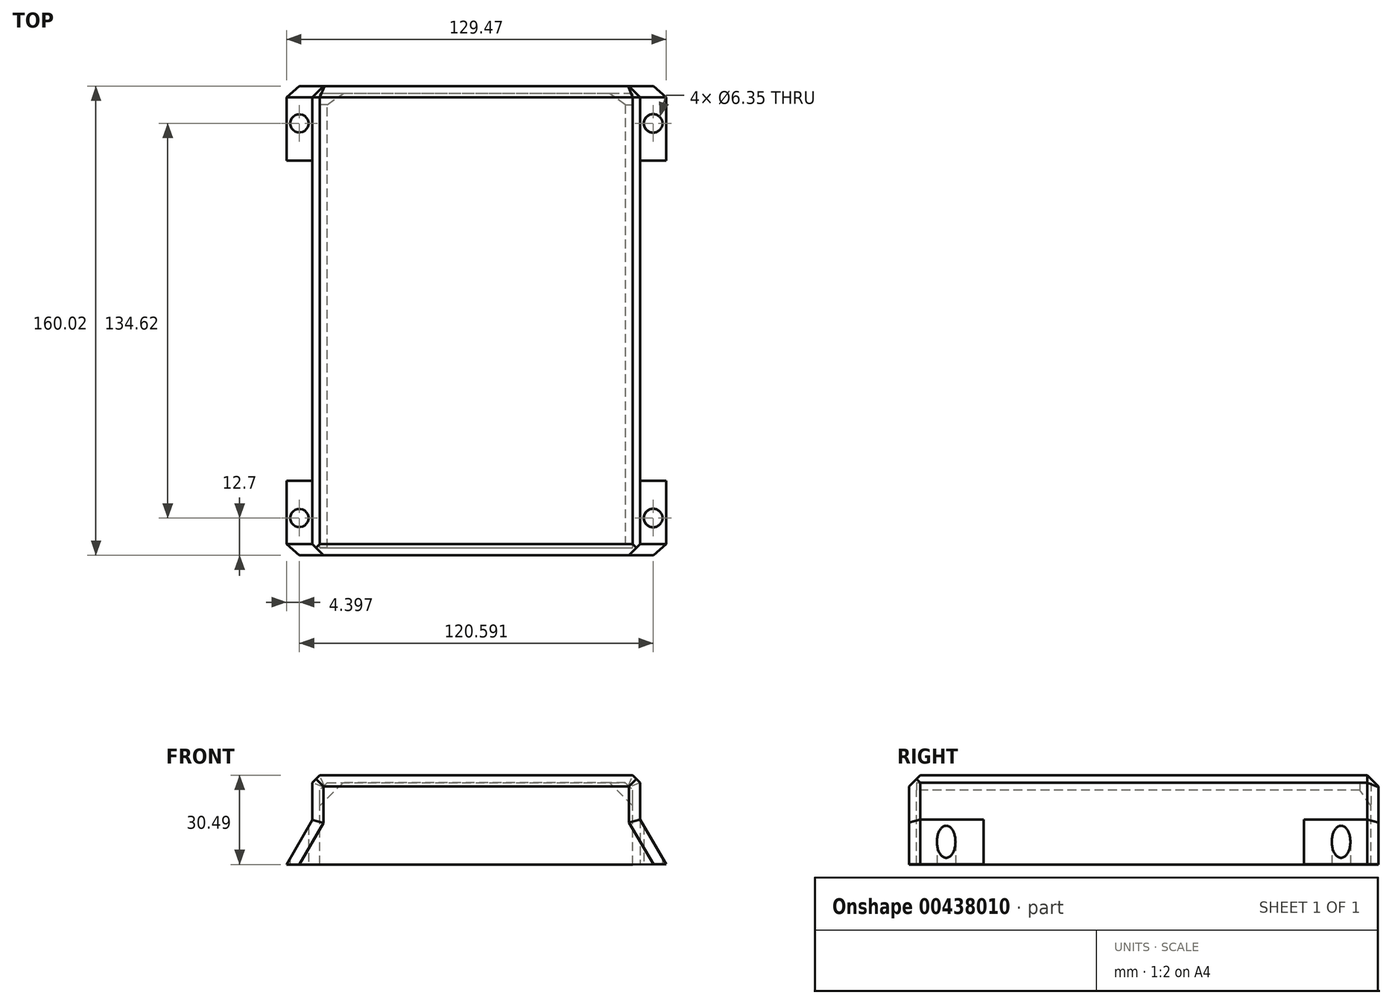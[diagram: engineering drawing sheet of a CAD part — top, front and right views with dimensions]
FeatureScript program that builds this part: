
annotation { "Feature Type Name" : "Feature", "Feature Type Description" : "" }
export const myFeature = defineFeature(function(context is Context, id is Id, definition is map)
    precondition{}
    {
        {
            var Q0;
            Q0=qCreatedBy(makeId("Front.planeOp"),FACE);
            var sketch = newSketch(context, id + "F0", { "sketchPlane" : qUnion([Q0])});
            skLineSegment(sketch, "E0.bottom", {"start": v(-84.5, 54.95) * mm, "end": v(27.26, 54.95) * mm});
            skLineSegment(sketch, "E0.top", {"start": v(-84.5, 24.47) * mm, "end": v(-81.96, 24.47) * mm});
            skLineSegment(sketch, "E0.left", {"start": v(-84.5, 54.95) * mm, "end": v(-84.5, 39.7) * mm});
            skLineSegment(sketch, "E0.right", {"start": v(27.26, 54.95) * mm, "end": v(27.26, 39.8) * mm});
            skLineSegment(sketch, "E1", {"start": v(-84.5, 39.7) * mm, "end": v(-93.3, 24.47) * mm});
            skLineSegment(sketch, "E2", {"start": v(-93.3, 24.47) * mm, "end": v(-84.5, 24.47) * mm});
            skLineSegment(sketch, "E3.MirrorCS", {"start": v(27.26, 39.8) * mm, "end": v(36.17, 24.5) * mm});
            skPoint(sketch, "E4.start.orphan", {"position": v(-28.62, 24.47) * mm});
            skLineSegment(sketch, "E5", {"start": v(-81.96, 24.47) * mm, "end": v(-81.96, 52.4) * mm});
            skLineSegment(sketch, "E6", {"start": v(-81.96, 52.4) * mm, "end": v(24.72, 52.4) * mm});
            skLineSegment(sketch, "E7.MirrorCS", {"start": v(24.72, 24.46) * mm, "end": v(24.72, 52.4) * mm});
            skLineSegment(sketch, "E8", {"start": v(24.72, 24.46) * mm, "end": v(36.17, 24.5) * mm});
            skSolve(sketch);
        }
        {
            var Q0;
            Q0=makeQuery(id+"F0.imprint","IMPRINT",FACE,{"disambiguationData":[TD([[makeQuery(id+"F0.imprint","IMPRINT",EDGE,{"derivedFrom":sQuery(id+"F0.wireOp",EDGE,"E0.bottom")}),-1.0]])]});
            extrude(context, id + "F1", {"entities" : qUnion([Q0]), "depth" : 160.02 * mm});
        }
        {
            var Q0;
            Q0=makeQuery(id+"F1.opExtrude","SWEPT_EDGE",EDGE,{"disambiguationData":[OSD([sQuery(id+"F0.wireOp",EDGE,"E0.bottom"),sQuery(id+"F0.wireOp",EDGE,"E0.left")])]});
            var Q1;
            Q1=makeQuery(id+"F1.opExtrude","SWEPT_EDGE",EDGE,{"disambiguationData":[OSD([sQuery(id+"F0.wireOp",EDGE,"E6"),sQuery(id+"F0.wireOp",EDGE,"E7.MirrorCS")])]});
            var Q2;
            Q2=makeQuery(id+"F1.opExtrude","SWEPT_EDGE",EDGE,{"disambiguationData":[OSD([sQuery(id+"F0.wireOp",EDGE,"E5"),sQuery(id+"F0.wireOp",EDGE,"E6")])]});
            var Q3;
            Q3=makeQuery(id+"F1.opExtrude","SWEPT_EDGE",EDGE,{"disambiguationData":[OSD([sQuery(id+"F0.wireOp",EDGE,"E0.bottom"),sQuery(id+"F0.wireOp",EDGE,"E0.right")])]});
            chamfer(context, id + "F2", {"entities" : qUnion([Q0, Q1, Q2, Q3]), "width" : 2.54 * mm, "tangentPropagation" : true});
        }
        {
            var Q0;
            Q0=makeQuery(id+"F2DOVUVanhk7CML_1.boolean.opBoolean","MERGE",FACE,{"derivedFrom":[makeQuery(id+"F1.opExtrude","SWEPT_FACE",FACE,{"disambiguationData":[OSD([sQuery(id+"F0.wireOp",EDGE,"E0.top"),sQuery(id+"F0.wireOp",EDGE,"E2")])]}),makeQuery(id+"F1.opExtrude","SWEPT_FACE",FACE,{"disambiguationData":[OSD([sQuery(id+"F0.wireOp",EDGE,"2e7b0b60-ae61-4e8e-ab8d-efaa882fdc4c.trimOffspring")])]}),makeQuery(id+"F2DOVUVanhk7CML_1.opExtrude","SWEPT_FACE",FACE,{"disambiguationData":[OSD([sQuery(id+"F7f3OZNVjXZdd6c_1.wireOp",EDGE,"704NCxIe-Shb7-Pqu0-nzQe-OlCcpkSPJt9R.bottom")])]})]});
            var sketch = newSketch(context, id + "F3", { "sketchPlane" : qUnion([Q0])});
            skLineSegment(sketch, "E9.left", {"start": v(-99.5, 134.62) * mm, "end": v(-99.5, 33.02) * mm});
            skLineSegment(sketch, "E10.MirrorCS", {"start": v(42.26, 134.62) * mm, "end": v(42.26, 33.02) * mm});
            skLineSegment(sketch, "E11.bottom", {"start": v(-99.5, 134.62) * mm, "end": v(-84.5, 134.62) * mm});
            skLineSegment(sketch, "E11.top", {"start": v(-99.5, 25.4) * mm, "end": v(-84.5, 25.4) * mm});
            skLineSegment(sketch, "E11.left", {"start": v(-99.5, 134.62) * mm, "end": v(-99.5, 25.4) * mm});
            skLineSegment(sketch, "E11.right", {"start": v(-84.5, 134.62) * mm, "end": v(-84.5, 25.4) * mm});
            skLineSegment(sketch, "E12.bottom", {"start": v(42.26, 134.62) * mm, "end": v(27.26, 134.62) * mm});
            skLineSegment(sketch, "E12.top", {"start": v(42.26, 25.4) * mm, "end": v(27.26, 25.4) * mm});
            skLineSegment(sketch, "E12.left", {"start": v(42.26, 134.62) * mm, "end": v(42.26, 25.4) * mm});
            skLineSegment(sketch, "E12.right", {"start": v(27.26, 134.62) * mm, "end": v(27.26, 25.4) * mm});
            skSolve(sketch);
        }
        {
            var Q0;
            Q0=makeQuery(id+"F3.imprint","IMPRINT",FACE,{"disambiguationData":[TD([[makeQuery(id+"F3.imprint","IMPRINT",EDGE,{"derivedFrom":sQuery(id+"F3.wireOp",EDGE,"E9.bottom")}),-1.0]])]});
            var Q1;
            {var subQ0=sQuery(id+"F3.wireOp",EDGE,"E10.MirrorCS");Q1=makeQuery(id+"F3.imprint","IMPRINT",FACE,{"disambiguationData":[TD([[makeQuery(id+"F3.imprint","IMPRINT",EDGE,{"derivedFrom":subQ0}),-1.0]])]});}
            extrude(context, id + "F4", {"entities" : qUnion([Q0, Q1]), "operationType" : NewBodyOperationType.REMOVE, "oppositeDirection" : true, "depth" : 25.4 * mm});
        }
        {
            var Q0;
            Q0=makeQuery(id+"F3.imprint","IMPRINT",FACE,{"disambiguationData":[TD([[makeQuery(id+"F3.imprint","IMPRINT",EDGE,{"derivedFrom":sQuery(id+"F3.wireOp",EDGE,"E11.bottom")}),-1.0]])]});
            var Q1;
            Q1=makeQuery(id+"F3.imprint","IMPRINT",FACE,{"disambiguationData":[TD([[makeQuery(id+"F3.imprint","IMPRINT",EDGE,{"derivedFrom":sQuery(id+"F3.wireOp",EDGE,"E12.bottom")}),1.0]])]});
            extrude(context, id + "F5", {"entities" : qUnion([Q0, Q1]), "operationType" : NewBodyOperationType.REMOVE, "oppositeDirection" : true, "depth" : 25.4 * mm});
        }
        {
            var Q0;
            Q0=makeQuery(id+"F2DOVUVanhk7CML_1.boolean.opBoolean","MERGE",FACE,{"derivedFrom":[makeQuery(id+"F1.opExtrude","SWEPT_FACE",FACE,{"disambiguationData":[OSD([sQuery(id+"F0.wireOp",EDGE,"E0.top"),sQuery(id+"F0.wireOp",EDGE,"E2")])]}),makeQuery(id+"F1.opExtrude","SWEPT_FACE",FACE,{"disambiguationData":[OSD([sQuery(id+"F0.wireOp",EDGE,"2e7b0b60-ae61-4e8e-ab8d-efaa882fdc4c.trimOffspring")])]}),makeQuery(id+"F2DOVUVanhk7CML_1.opExtrude","SWEPT_FACE",FACE,{"disambiguationData":[OSD([sQuery(id+"F7f3OZNVjXZdd6c_1.wireOp",EDGE,"704NCxIe-Shb7-Pqu0-nzQe-OlCcpkSPJt9R.bottom")])]})]});
            var sketch = newSketch(context, id + "F6", { "sketchPlane" : qUnion([Q0])});
            skCircle(sketch, "E13", {"center": v(-88.9, 147.32) * mm, "radius": 3.18 * mm});
            skPoint(sketch, "E13.centerSnap0", {"position": v(-93.3, 147.32) * mm});
            skPoint(sketch, "E13.centerSnap1", {"position": v(-88.9, 134.62) * mm});
            skCircle(sketch, "E14", {"center": v(-88.9, 12.7) * mm, "radius": 3.18 * mm});
            skPoint(sketch, "E14.centerSnap0", {"position": v(-88.9, 25.4) * mm});
            skPoint(sketch, "E14.centerSnap1", {"position": v(-93.3, 12.7) * mm});
            skSolve(sketch);
        }
        {
            var Q0;
            Q0=makeQuery(id+"F6.imprint","IMPRINT",FACE,{"disambiguationData":[TD([[makeQuery(id+"F6.imprint","IMPRINT",EDGE,{"derivedFrom":sQuery(id+"F6.wireOp",EDGE,"E14")}),1.0]])]});
            var Q1;
            Q1=makeQuery(id+"F6.imprint","IMPRINT",FACE,{"disambiguationData":[TD([[makeQuery(id+"F6.imprint","IMPRINT",EDGE,{"derivedFrom":sQuery(id+"F6.wireOp",EDGE,"E13")}),1.0]])]});
            var Q2;
            Q2=makeQuery(id+"FXtNLgF4TMoL3fm_1.imprint","IMPRINT",FACE,{"disambiguationData":[TD([[makeQuery(id+"FXtNLgF4TMoL3fm_1.imprint","IMPRINT",EDGE,{"derivedFrom":sQuery(id+"FXtNLgF4TMoL3fm_1.wireOp",EDGE,"AvXykiR3-Juc4-Uzjr-7NnA-D4NbyHo4XRPa")}),1.0]])]});
            var Q3;
            Q3=makeQuery(id+"FY5yyZJvRh9AwFM_1.imprint","IMPRINT",FACE,{"disambiguationData":[TD([[makeQuery(id+"FY5yyZJvRh9AwFM_1.imprint","IMPRINT",EDGE,{"derivedFrom":sQuery(id+"FY5yyZJvRh9AwFM_1.wireOp",EDGE,"1o40Q4Pv-ev4r-qfsh-RZnV-3lQHRS0gfTlM")}),1.0]])]});
            extrude(context, id + "F7", {"entities" : qUnion([Q0, Q1, Q2, Q3]), "operationType" : NewBodyOperationType.REMOVE, "oppositeDirection" : true, "depth" : 25.4 * mm});
        }
        {
            var Q0;
            Q0=makeQuery(id+"F1.opExtrude","CAP_FACE",FACE,{"disambiguationData":[OSD([sQuery(id+"F0.wireOp",EDGE,"E0.bottom"),sQuery(id+"F0.wireOp",EDGE,"E0.top"),sQuery(id+"F0.wireOp",EDGE,"E0.left"),sQuery(id+"F0.wireOp",EDGE,"E0.right"),sQuery(id+"F0.wireOp",EDGE,"E1"),sQuery(id+"F0.wireOp",EDGE,"E2"),sQuery(id+"F0.wireOp",EDGE,"E3.MirrorCS"),sQuery(id+"F0.wireOp",EDGE,"E5"),sQuery(id+"F0.wireOp",EDGE,"E6"),sQuery(id+"F0.wireOp",EDGE,"E7.MirrorCS"),sQuery(id+"F0.wireOp",EDGE,"E8")])],"isStart":false});
            var sketch = newSketch(context, id + "F8", { "sketchPlane" : qUnion([Q0])});
            skLineSegment(sketch, "E15.bottom", {"start": v(-81.96, 24.47) * mm, "end": v(24.72, 24.47) * mm});
            skLineSegment(sketch, "E15.top", {"start": v(-81.96, 52.4) * mm, "end": v(24.72, 52.4) * mm});
            skLineSegment(sketch, "E15.left", {"start": v(-81.96, 24.47) * mm, "end": v(-81.96, 52.4) * mm});
            skLineSegment(sketch, "E15.right", {"start": v(24.72, 24.47) * mm, "end": v(24.72, 52.4) * mm});
            skSolve(sketch);
        }
        {
            var Q0;
            {var subQ8=sQuery(id+"F8.wireOp",EDGE,"E15.bottom");Q0=makeQuery(id+"F8.imprint","IMPRINT",FACE,{"disambiguationData":[TD([[makeQuery(id+"F8.imprint","IMPRINT",EDGE,{"derivedFrom":subQ8}),1.0]])]});}
            extrude(context, id + "F9", {"entities" : qUnion([Q0]), "operationType" : NewBodyOperationType.ADD, "oppositeDirection" : true, "depth" : 2.54 * mm});
        }
        {
            var Q0;
            Q0=makeQuery(id+"F1.opExtrude","SWEPT_FACE",FACE,{"disambiguationData":[OSD([sQuery(id+"F0.wireOp",EDGE,"E8")])]});
            var sketch = newSketch(context, id + "F10", { "sketchPlane" : qUnion([Q0])});
            skCircle(sketch, "E16", {"center": v(31.8, 147.32) * mm, "radius": 3.18 * mm});
            skPoint(sketch, "E16.centerSnap0", {"position": v(31.8, 134.62) * mm});
            skPoint(sketch, "E16.centerSnap1", {"position": v(36.26, 147.32) * mm});
            skCircle(sketch, "E17", {"center": v(31.8, 12.7) * mm, "radius": 3.18 * mm});
            skPoint(sketch, "E17.centerSnap0", {"position": v(36.26, 12.7) * mm});
            skPoint(sketch, "E17.centerSnap1", {"position": v(30.53, 0) * mm});
            skPoint(sketch, "E18", {"position": v(31.8, 25.4) * mm});
            skSolve(sketch);
        }
        {
            var Q0;
            Q0=qSketchRegion(id+"F10",true);
            extrude(context, id + "F11", {"entities" : qUnion([Q0]), "operationType" : NewBodyOperationType.REMOVE, "oppositeDirection" : true, "depth" : 25.4 * mm});
        }
        {
            var Q0;
            Q0=makeQuery(id+"F1.opExtrude","CAP_EDGE",EDGE,{"disambiguationData":[OSD([sQuery(id+"F0.wireOp",EDGE,"E3.MirrorCS")])],"isStart":false});
            var Q1;
            Q1=makeQuery(id+"F1.opExtrude","CAP_EDGE",EDGE,{"disambiguationData":[OSD([sQuery(id+"F0.wireOp",EDGE,"E0.right")])],"isStart":false});
            var Q2;
            Q2=makeQuery(id+"F1.opExtrude","CAP_EDGE",EDGE,{"disambiguationData":[OSD([sQuery(id+"F0.wireOp",EDGE,"E1")])],"isStart":false});
            var Q3;
            Q3=makeQuery(id+"F1.opExtrude","CAP_EDGE",EDGE,{"disambiguationData":[OSD([sQuery(id+"F0.wireOp",EDGE,"E0.left")])],"isStart":false});
            var Q4;
            Q4=makeQuery(id+"F9.opExtrude","CAP_EDGE",EDGE,{"disambiguationData":[OSD([sQuery(id+"F8.wireOp",EDGE,"E15.right")])],"isStart":false});
            var Q5;
            Q5=makeQuery(id+"F9.opExtrude","CAP_EDGE",EDGE,{"disambiguationData":[OSD([sQuery(id+"F8.wireOp",EDGE,"E15.left")])],"isStart":false});
            var Q6;
            Q6=makeQuery(id+"F1.opExtrude","CAP_EDGE",EDGE,{"disambiguationData":[OSD([sQuery(id+"F0.wireOp",EDGE,"E0.bottom")])],"isStart":false});
            var Q7;
            Q7=makeQuery(id+"F9.opExtrude","CAP_EDGE",EDGE,{"disambiguationData":[OSD([sQuery(id+"F8.wireOp",EDGE,"E15.top")])],"isStart":false});
            chamfer(context, id + "F12", {"entities" : qUnion([Q0, Q1, Q2, Q3, Q4, Q5, Q6, Q7]), "width" : 3.8 * mm, "tangentPropagation" : true});
        }
        {
            var Q0;
            Q0=makeQuery(id+"F1.opExtrude","CAP_FACE",FACE,{"disambiguationData":[OSD([sQuery(id+"F0.wireOp",EDGE,"E0.bottom"),sQuery(id+"F0.wireOp",EDGE,"E0.top"),sQuery(id+"F0.wireOp",EDGE,"E0.left"),sQuery(id+"F0.wireOp",EDGE,"E0.right"),sQuery(id+"F0.wireOp",EDGE,"E1"),sQuery(id+"F0.wireOp",EDGE,"E2"),sQuery(id+"F0.wireOp",EDGE,"E3.MirrorCS"),sQuery(id+"F0.wireOp",EDGE,"E5"),sQuery(id+"F0.wireOp",EDGE,"E6"),sQuery(id+"F0.wireOp",EDGE,"E7.MirrorCS"),sQuery(id+"F0.wireOp",EDGE,"E8")])],"isStart":true});
            var sketch = newSketch(context, id + "F13", { "sketchPlane" : qUnion([Q0])});
            skLineSegment(sketch, "E19.bottom", {"start": v(-24.72, 24.46) * mm, "end": v(81.96, 24.46) * mm});
            skLineSegment(sketch, "E19.top", {"start": v(-24.72, 52.4) * mm, "end": v(81.96, 52.4) * mm});
            skLineSegment(sketch, "E19.left", {"start": v(-24.72, 24.46) * mm, "end": v(-24.72, 52.4) * mm});
            skLineSegment(sketch, "E19.right", {"start": v(81.96, 24.46) * mm, "end": v(81.96, 52.4) * mm});
            skSolve(sketch);
        }
        {
            var Q0;
            Q0=qSketchRegion(id+"F13",true);
            extrude(context, id + "F14", {"entities" : qUnion([Q0]), "operationType" : NewBodyOperationType.ADD, "oppositeDirection" : true, "depth" : 2.54 * mm});
        }
        {
            var Q0;
            Q0=makeQuery(id+"F1.opExtrude","CAP_EDGE",EDGE,{"disambiguationData":[OSD([sQuery(id+"F0.wireOp",EDGE,"E3.MirrorCS")])],"isStart":true});
            var Q1;
            Q1=makeQuery(id+"F1.opExtrude","CAP_EDGE",EDGE,{"disambiguationData":[OSD([sQuery(id+"F0.wireOp",EDGE,"E0.right")])],"isStart":true});
            var Q2;
            {var subQ0=sQuery(id+"F0.wireOp",EDGE,"E0.right");var subQ1=sQuery(id+"F0.wireOp",EDGE,"E0.bottom");Q2=makeQuery(id+"F2.opChamfer","BLEND_EDGE",EDGE,{"blendedFrom":[makeQuery(id+"F1.opExtrude","SWEPT_EDGE",EDGE,{"disambiguationData":[OSD([subQ1,subQ0])]}),makeQuery(id+"F1.opExtrude","CAP_FACE",FACE,{"disambiguationData":[OSD([subQ1,sQuery(id+"F0.wireOp",EDGE,"E0.top"),sQuery(id+"F0.wireOp",EDGE,"E0.left"),subQ0,sQuery(id+"F0.wireOp",EDGE,"E1"),sQuery(id+"F0.wireOp",EDGE,"E2"),sQuery(id+"F0.wireOp",EDGE,"E3.MirrorCS"),sQuery(id+"F0.wireOp",EDGE,"E5"),sQuery(id+"F0.wireOp",EDGE,"E6"),sQuery(id+"F0.wireOp",EDGE,"E7.MirrorCS"),sQuery(id+"F0.wireOp",EDGE,"E8")])],"isStart":true})],"blendedInto":[makeQuery(id+"F1.opExtrude","CAP_FACE",FACE,{"disambiguationData":[OSD([subQ1,sQuery(id+"F0.wireOp",EDGE,"E0.top"),sQuery(id+"F0.wireOp",EDGE,"E0.left"),subQ0,sQuery(id+"F0.wireOp",EDGE,"E1"),sQuery(id+"F0.wireOp",EDGE,"E2"),sQuery(id+"F0.wireOp",EDGE,"E3.MirrorCS"),sQuery(id+"F0.wireOp",EDGE,"E5"),sQuery(id+"F0.wireOp",EDGE,"E6"),sQuery(id+"F0.wireOp",EDGE,"E7.MirrorCS"),sQuery(id+"F0.wireOp",EDGE,"E8")])],"isStart":true})]});}
            var Q3;
            Q3=makeQuery(id+"F1.opExtrude","CAP_EDGE",EDGE,{"disambiguationData":[OSD([sQuery(id+"F0.wireOp",EDGE,"E0.bottom")])],"isStart":true});
            var Q4;
            {var subQ0=sQuery(id+"F0.wireOp",EDGE,"E0.left");var subQ1=sQuery(id+"F0.wireOp",EDGE,"E0.bottom");Q4=makeQuery(id+"F2.opChamfer","BLEND_EDGE",EDGE,{"blendedFrom":[makeQuery(id+"F1.opExtrude","SWEPT_EDGE",EDGE,{"disambiguationData":[OSD([subQ1,subQ0])]}),makeQuery(id+"F1.opExtrude","CAP_FACE",FACE,{"disambiguationData":[OSD([subQ1,sQuery(id+"F0.wireOp",EDGE,"E0.top"),subQ0,sQuery(id+"F0.wireOp",EDGE,"E0.right"),sQuery(id+"F0.wireOp",EDGE,"E1"),sQuery(id+"F0.wireOp",EDGE,"E2"),sQuery(id+"F0.wireOp",EDGE,"E3.MirrorCS"),sQuery(id+"F0.wireOp",EDGE,"E5"),sQuery(id+"F0.wireOp",EDGE,"E6"),sQuery(id+"F0.wireOp",EDGE,"E7.MirrorCS"),sQuery(id+"F0.wireOp",EDGE,"E8")])],"isStart":true})],"blendedInto":[makeQuery(id+"F1.opExtrude","CAP_FACE",FACE,{"disambiguationData":[OSD([subQ1,sQuery(id+"F0.wireOp",EDGE,"E0.top"),subQ0,sQuery(id+"F0.wireOp",EDGE,"E0.right"),sQuery(id+"F0.wireOp",EDGE,"E1"),sQuery(id+"F0.wireOp",EDGE,"E2"),sQuery(id+"F0.wireOp",EDGE,"E3.MirrorCS"),sQuery(id+"F0.wireOp",EDGE,"E5"),sQuery(id+"F0.wireOp",EDGE,"E6"),sQuery(id+"F0.wireOp",EDGE,"E7.MirrorCS"),sQuery(id+"F0.wireOp",EDGE,"E8")])],"isStart":true})]});}
            var Q5;
            Q5=makeQuery(id+"F1.opExtrude","CAP_EDGE",EDGE,{"disambiguationData":[OSD([sQuery(id+"F0.wireOp",EDGE,"E0.left")])],"isStart":true});
            var Q6;
            Q6=makeQuery(id+"F1.opExtrude","CAP_EDGE",EDGE,{"disambiguationData":[OSD([sQuery(id+"F0.wireOp",EDGE,"E1")])],"isStart":true});
            var Q7;
            Q7=makeQuery(id+"F14.opExtrude","CAP_EDGE",EDGE,{"disambiguationData":[OSD([sQuery(id+"F13.wireOp",EDGE,"E19.top")])],"isStart":false});
            var Q8;
            Q8=makeQuery(id+"F14.opExtrude","CAP_EDGE",EDGE,{"disambiguationData":[OSD([sQuery(id+"F13.wireOp",EDGE,"E19.left")])],"isStart":false});
            var Q9;
            Q9=makeQuery(id+"F14.boolean.opBoolean","INTERSECT",EDGE,{"derivedFrom":[makeQuery(id+"F2.opChamfer","BLEND_FACE",FACE,{"disambiguationData":[OSD([sQuery(id+"F0.wireOp",EDGE,"E6"),sQuery(id+"F0.wireOp",EDGE,"E7.MirrorCS")])]}),makeQuery(id+"F14.opExtrude","CAP_FACE",FACE,{"disambiguationData":[OSD([sQuery(id+"F13.wireOp",EDGE,"E19.bottom"),sQuery(id+"F13.wireOp",EDGE,"E19.top"),sQuery(id+"F13.wireOp",EDGE,"E19.left"),sQuery(id+"F13.wireOp",EDGE,"E19.right")])],"isStart":false})]});
            var Q10;
            Q10=makeQuery(id+"F14.boolean.opBoolean","INTERSECT",EDGE,{"derivedFrom":[makeQuery(id+"F2.opChamfer","BLEND_FACE",FACE,{"disambiguationData":[OSD([sQuery(id+"F0.wireOp",EDGE,"E5"),sQuery(id+"F0.wireOp",EDGE,"E6")])]}),makeQuery(id+"F14.opExtrude","CAP_FACE",FACE,{"disambiguationData":[OSD([sQuery(id+"F13.wireOp",EDGE,"E19.bottom"),sQuery(id+"F13.wireOp",EDGE,"E19.top"),sQuery(id+"F13.wireOp",EDGE,"E19.left"),sQuery(id+"F13.wireOp",EDGE,"E19.right")])],"isStart":false})]});
            var Q11;
            {var subQ0=sQuery(id+"F13.wireOp",EDGE,"E19.right");Q11=makeQuery(id+"F14.boolean.opBoolean","SPLIT",EDGE,{"disambiguationData":[topologyDisambiguationEdgeConnected([makeQuery(id+"F1.opExtrude","SWEPT_FACE",FACE,{"disambiguationData":[OSD([sQuery(id+"F0.wireOp",EDGE,"E5")])]})])],"derivedFrom":makeQuery(id+"F14.opExtrude","CAP_EDGE",EDGE,{"disambiguationData":[OSD([subQ0])],"isStart":false})});}
            chamfer(context, id + "F15", {"entities" : qUnion([Q0, Q1, Q2, Q3, Q4, Q5, Q6, Q7, Q8, Q9, Q10, Q11]), "width" : 3.8 * mm, "tangentPropagation" : true});
        }
    });
